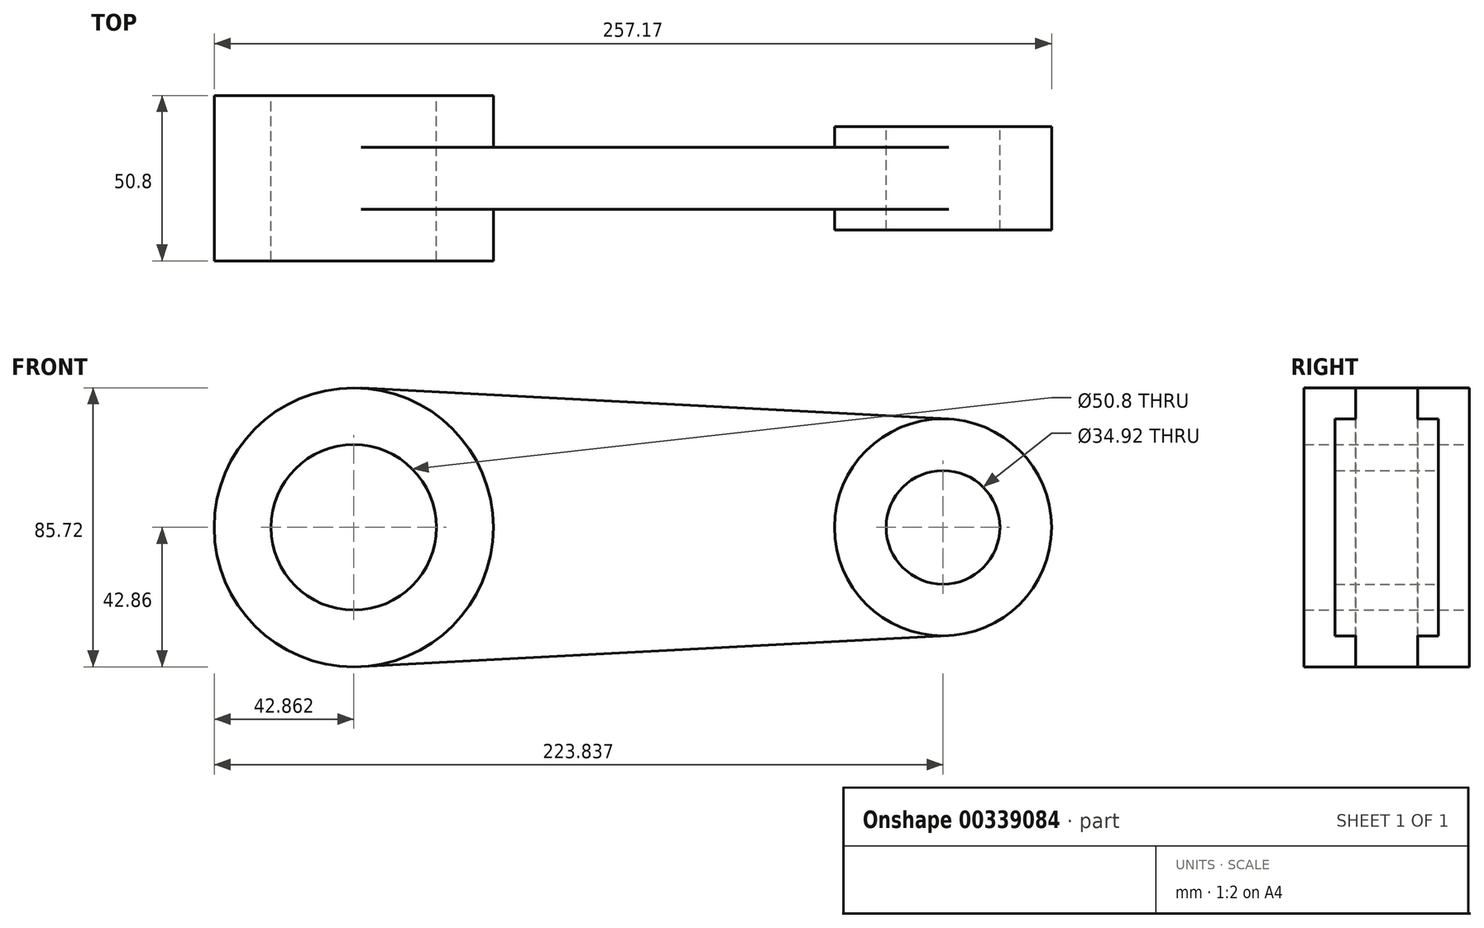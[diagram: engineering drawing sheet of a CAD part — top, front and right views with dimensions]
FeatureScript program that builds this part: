
annotation { "Feature Type Name" : "Feature", "Feature Type Description" : "" }
export const myFeature = defineFeature(function(context is Context, id is Id, definition is map)
    precondition{}
    {
        {
            var Q0;
            Q0=qCreatedBy(makeId("Front.planeOp"),FACE);
            var sketch = newSketch(context, id + "F0", { "sketchPlane" : qUnion([Q0])});
            skCircle(sketch, "E0", {"center": v(-104.28, 0) * mm, "radius": 25.4 * mm});
            skCircle(sketch, "E1", {"center": v(76.7, 0) * mm, "radius": 17.46 * mm});
            skCircle(sketch, "E2", {"center": v(76.7, 0) * mm, "radius": 33.34 * mm});
            skCircle(sketch, "E3", {"center": v(-104.28, 0) * mm, "radius": 42.86 * mm});
            skLineSegment(sketch, "E4", {"start": v(-102.02, 42.8) * mm, "end": v(78.45, 33.3) * mm});
            skLineSegment(sketch, "E5", {"start": v(-102.02, -42.8) * mm, "end": v(78.45, -33.3) * mm});
            skSolve(sketch);
        }
        {
            var Q0;
            {var subQ0=sQuery(id+"F0.wireOp",EDGE,"E4");Q0=makeQuery(id+"F0.imprint","IMPRINT",FACE,{"disambiguationData":[TD([[makeQuery(id+"F0.imprint","IMPRINT",EDGE,{"derivedFrom":subQ0}),-1.0]])]});}
            extrude(context, id + "F1", {"entities" : qUnion([Q0]), "depth" : 19.05 * mm, "symmetric" : true});
        }
        {
            var Q0;
            Q0=makeQuery(id+"F0.imprint","IMPRINT",FACE,{"disambiguationData":[TD([[makeQuery(id+"F0.imprint","IMPRINT",EDGE,{"derivedFrom":sQuery(id+"F0.wireOp",EDGE,"E0")}),-1.0]])]});
            extrude(context, id + "F2", {"entities" : qUnion([Q0]), "operationType" : NewBodyOperationType.ADD, "depth" : 50.8 * mm, "symmetric" : true});
        }
        {
            var Q0;
            Q0=makeQuery(id+"F0.imprint","IMPRINT",FACE,{"disambiguationData":[TD([[makeQuery(id+"F0.imprint","IMPRINT",EDGE,{"derivedFrom":sQuery(id+"F0.wireOp",EDGE,"E1")}),-1.0]])]});
            extrude(context, id + "F3", {"entities" : qUnion([Q0]), "operationType" : NewBodyOperationType.ADD, "depth" : 31.75 * mm, "symmetric" : true});
        }
    });
